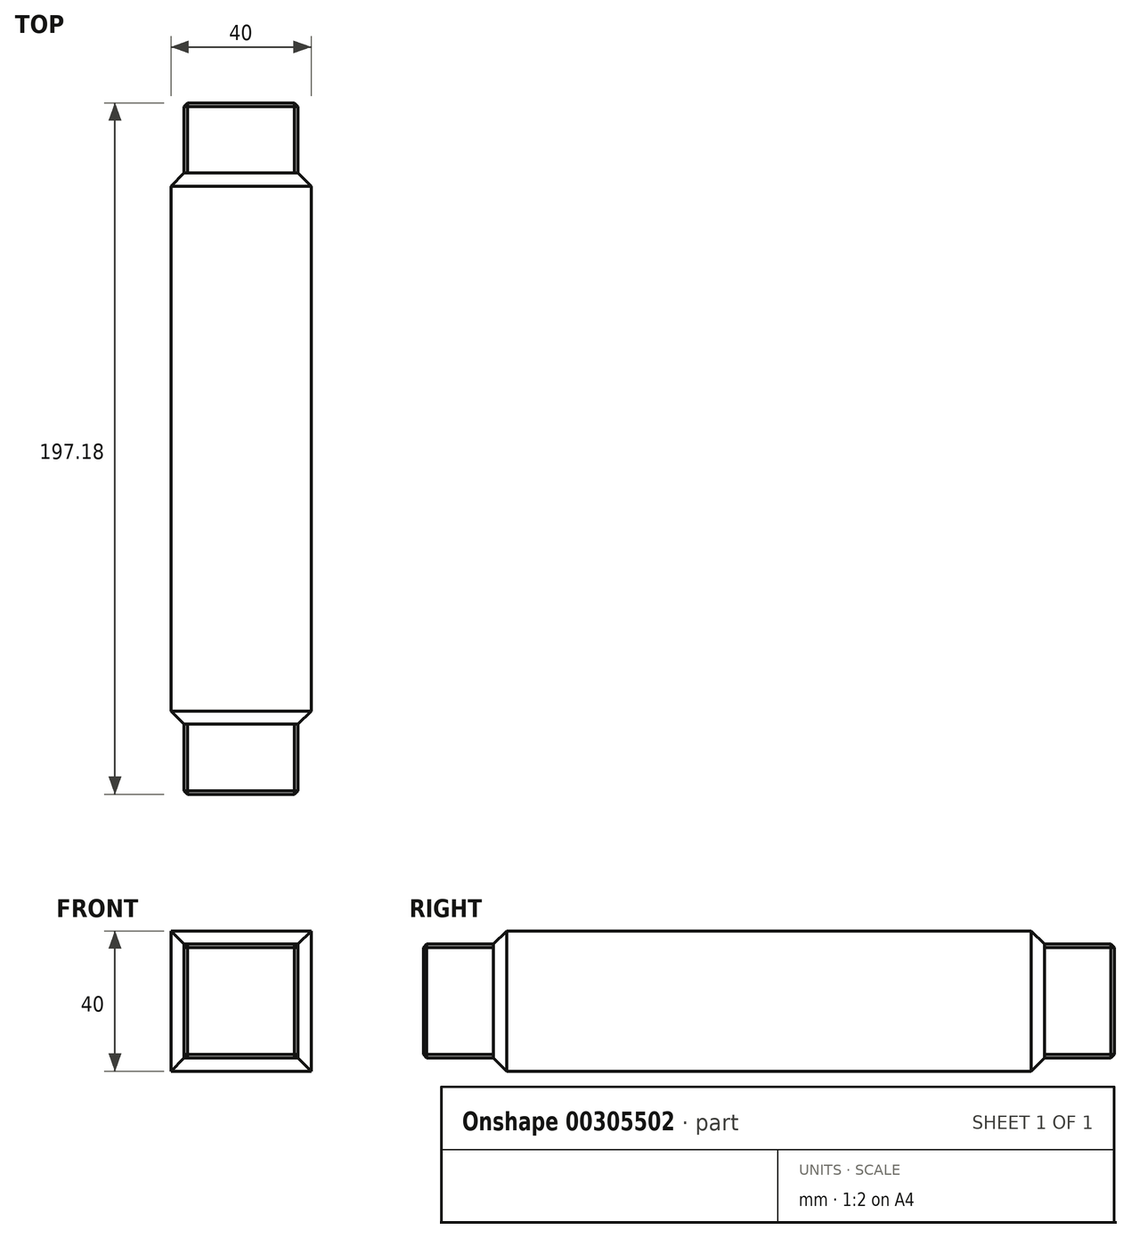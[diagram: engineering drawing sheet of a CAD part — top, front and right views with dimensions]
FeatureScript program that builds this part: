
annotation { "Feature Type Name" : "Feature", "Feature Type Description" : "" }
export const myFeature = defineFeature(function(context is Context, id is Id, definition is map)
    precondition{}
    {
        {
            var Q0;
            Q0=qCreatedBy(makeId("Right.planeOp"),FACE);
            var sketch = newSketch(context, id + "F0", { "sketchPlane" : qUnion([Q0])});
            skLineSegment(sketch, "E0.bottom", {"start": v(78.6, 20) * mm, "end": v(-78.6, 20) * mm});
            skLineSegment(sketch, "E0.top", {"start": v(78.6, -20) * mm, "end": v(-78.6, -20) * mm});
            skLineSegment(sketch, "E0.left", {"start": v(78.6, 20) * mm, "end": v(78.6, -20) * mm});
            skLineSegment(sketch, "E0.right", {"start": v(-78.6, 20) * mm, "end": v(-78.6, -20) * mm});
            skPoint(sketch, "E0.middle", {"position": v(0, 0) * mm});
            skSolve(sketch);
        }
        {
            var Q0;
            Q0=makeQuery(id+"F0.imprint","IMPRINT",FACE,{"disambiguationData":[TD([[makeQuery(id+"F0.imprint","IMPRINT",EDGE,{"derivedFrom":sQuery(id+"F0.wireOp",EDGE,"E0.bottom")}),1.0]])]});
            extrude(context, id + "F1", {"entities" : qUnion([Q0]), "endBound" : BoundingType.SYMMETRIC, "depth" : 40 * mm});
        }
        {
            var Q0;
            Q0=qCreatedBy(makeId("Right.planeOp"),FACE);
            var sketch = newSketch(context, id + "F2", { "sketchPlane" : qUnion([Q0])});
            skLineSegment(sketch, "E1", {"start": v(0, 0) * mm, "end": v(-88.6, 0) * mm, "construction": true});
            skLineSegment(sketch, "E2.bottom", {"start": v(-78.6, 16.25) * mm, "end": v(-98.6, 16.25) * mm});
            skLineSegment(sketch, "E2.top", {"start": v(-78.6, -16.25) * mm, "end": v(-98.6, -16.25) * mm});
            skLineSegment(sketch, "E2.left", {"start": v(-78.6, 16.25) * mm, "end": v(-78.6, -16.25) * mm});
            skLineSegment(sketch, "E2.right", {"start": v(-98.6, 16.25) * mm, "end": v(-98.6, -16.25) * mm});
            skPoint(sketch, "E2.middle", {"position": v(-88.6, 0) * mm});
            skLineSegment(sketch, "E3.MirrorCS", {"start": v(98.6, 16.25) * mm, "end": v(98.6, -16.25) * mm});
            skLineSegment(sketch, "E4.MirrorCS", {"start": v(78.6, 16.25) * mm, "end": v(78.6, -16.25) * mm});
            skLineSegment(sketch, "E5.MirrorCS", {"start": v(78.6, -16.25) * mm, "end": v(98.6, -16.25) * mm});
            skLineSegment(sketch, "E6.MirrorCS", {"start": v(78.6, 16.25) * mm, "end": v(98.6, 16.25) * mm});
            skPoint(sketch, "E7.MirrorP", {"position": v(88.6, 0) * mm});
            skSolve(sketch);
        }
        {
            var Q0;
            Q0=makeQuery(id+"F2.imprint","IMPRINT",FACE,{"disambiguationData":[TD([[makeQuery(id+"F2.imprint","IMPRINT",EDGE,{"derivedFrom":sQuery(id+"F2.wireOp",EDGE,"E2.bottom")}),1.0]])]});
            var Q1;
            Q1=makeQuery(id+"F2.imprint","IMPRINT",FACE,{"disambiguationData":[TD([[makeQuery(id+"F2.imprint","IMPRINT",EDGE,{"derivedFrom":sQuery(id+"F2.wireOp",EDGE,"E3.MirrorCS")}),-1.0]])]});
            extrude(context, id + "F3", {"entities" : qUnion([Q0, Q1]), "operationType" : NewBodyOperationType.ADD, "endBound" : BoundingType.SYMMETRIC, "depth" : 32.5 * mm});
        }
        {
            var Q0;
            Q0=makeQuery(id+"F3.opExtrude","SWEPT_FACE",FACE,{"disambiguationData":[OSD([sQuery(id+"F2.wireOp",EDGE,"E2.right")])]});
            var Q1;
            Q1=makeQuery(id+"F3.opExtrude","CAP_EDGE",EDGE,{"disambiguationData":[OSD([sQuery(id+"F2.wireOp",EDGE,"E2.bottom")])],"isStart":false});
            var Q2;
            Q2=makeQuery(id+"F3.opExtrude","CAP_EDGE",EDGE,{"disambiguationData":[OSD([sQuery(id+"F2.wireOp",EDGE,"E2.bottom")])],"isStart":true});
            var Q3;
            Q3=makeQuery(id+"F3.opExtrude","CAP_EDGE",EDGE,{"disambiguationData":[OSD([sQuery(id+"F2.wireOp",EDGE,"E2.top")])],"isStart":false});
            var Q4;
            Q4=makeQuery(id+"F3.opExtrude","CAP_EDGE",EDGE,{"disambiguationData":[OSD([sQuery(id+"F2.wireOp",EDGE,"E6.MirrorCS")])],"isStart":true});
            var Q5;
            Q5=makeQuery(id+"F3.opExtrude","CAP_EDGE",EDGE,{"disambiguationData":[OSD([sQuery(id+"F2.wireOp",EDGE,"E6.MirrorCS")])],"isStart":false});
            var Q6;
            Q6=makeQuery(id+"F3.opExtrude","CAP_EDGE",EDGE,{"disambiguationData":[OSD([sQuery(id+"F2.wireOp",EDGE,"E5.MirrorCS")])],"isStart":false});
            var Q7;
            Q7=makeQuery(id+"F3.opExtrude","CAP_EDGE",EDGE,{"disambiguationData":[OSD([sQuery(id+"F2.wireOp",EDGE,"E5.MirrorCS")])],"isStart":true});
            var Q8;
            Q8=makeQuery(id+"F3.opExtrude","CAP_EDGE",EDGE,{"disambiguationData":[OSD([sQuery(id+"F2.wireOp",EDGE,"E2.top")])],"isStart":true});
            var Q9;
            Q9=makeQuery(id+"F3.opExtrude","SWEPT_FACE",FACE,{"disambiguationData":[OSD([sQuery(id+"F2.wireOp",EDGE,"E3.MirrorCS")])]});
            chamfer(context, id + "F4", {"entities" : qUnion([Q0, Q1, Q2, Q3, Q4, Q5, Q6, Q7, Q8, Q9]), "width" : 1 * mm, "tangentPropagation" : true});
        }
        {
            var Q0;
            Q0=makeQuery(id+"F1.opExtrude","SWEPT_EDGE",EDGE,{"disambiguationData":[OSD([sQuery(id+"F0.wireOp",EDGE,"E0.bottom"),sQuery(id+"F0.wireOp",EDGE,"E0.left")])]});
            var Q1;
            Q1=makeQuery(id+"F1.opExtrude","CAP_EDGE",EDGE,{"disambiguationData":[OSD([sQuery(id+"F0.wireOp",EDGE,"E0.left")])],"isStart":true});
            var Q2;
            Q2=makeQuery(id+"F1.opExtrude","SWEPT_EDGE",EDGE,{"disambiguationData":[OSD([sQuery(id+"F0.wireOp",EDGE,"E0.top"),sQuery(id+"F0.wireOp",EDGE,"E0.left")])]});
            var Q3;
            Q3=makeQuery(id+"F1.opExtrude","CAP_EDGE",EDGE,{"disambiguationData":[OSD([sQuery(id+"F0.wireOp",EDGE,"E0.left")])],"isStart":false});
            var Q4;
            Q4=makeQuery(id+"F1.opExtrude","CAP_EDGE",EDGE,{"disambiguationData":[OSD([sQuery(id+"F0.wireOp",EDGE,"E0.right")])],"isStart":false});
            var Q5;
            Q5=makeQuery(id+"F1.opExtrude","SWEPT_EDGE",EDGE,{"disambiguationData":[OSD([sQuery(id+"F0.wireOp",EDGE,"E0.bottom"),sQuery(id+"F0.wireOp",EDGE,"E0.right")])]});
            var Q6;
            Q6=makeQuery(id+"F1.opExtrude","CAP_EDGE",EDGE,{"disambiguationData":[OSD([sQuery(id+"F0.wireOp",EDGE,"E0.right")])],"isStart":true});
            var Q7;
            Q7=makeQuery(id+"F1.opExtrude","SWEPT_EDGE",EDGE,{"disambiguationData":[OSD([sQuery(id+"F0.wireOp",EDGE,"E0.top"),sQuery(id+"F0.wireOp",EDGE,"E0.right")])]});
            chamfer(context, id + "F5", {"entities" : qUnion([Q0, Q1, Q2, Q3, Q4, Q5, Q6, Q7]), "width" : 3.75 * mm, "tangentPropagation" : true});
        }
    });
